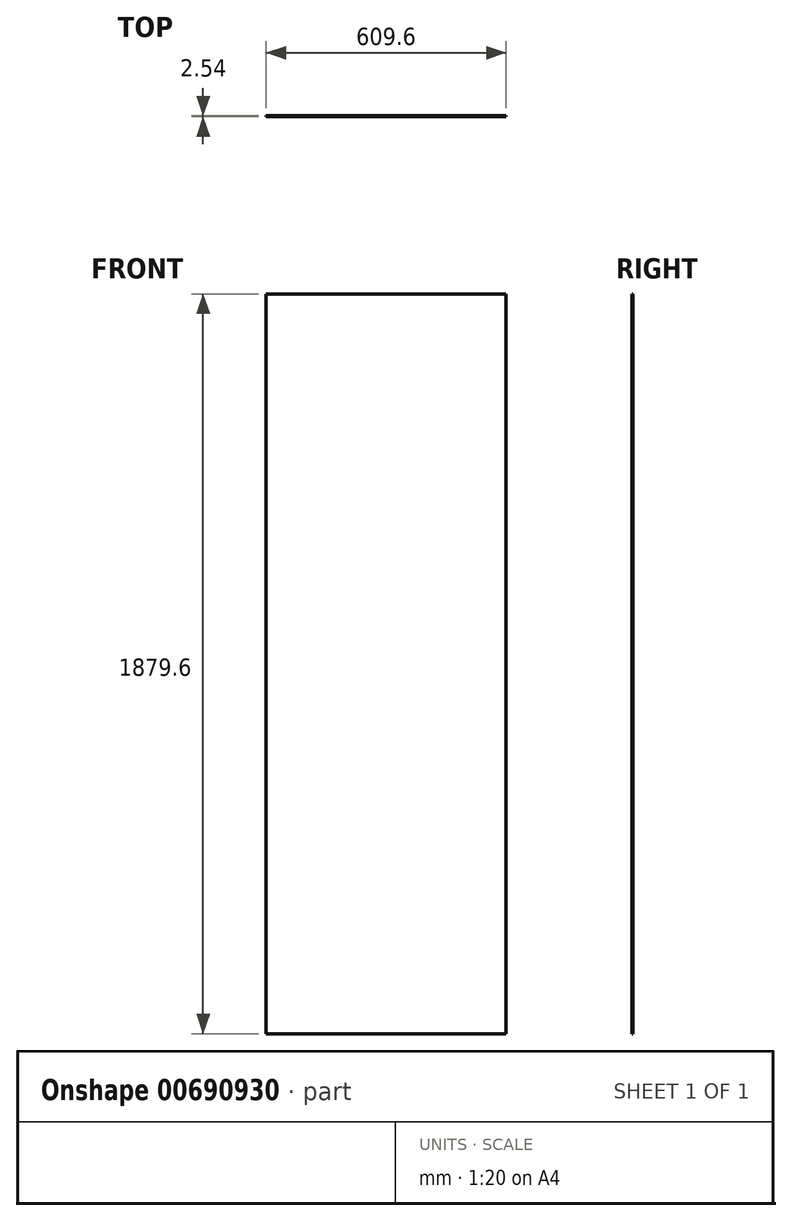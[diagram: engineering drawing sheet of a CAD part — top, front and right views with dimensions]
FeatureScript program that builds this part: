
annotation { "Feature Type Name" : "Feature", "Feature Type Description" : "" }
export const myFeature = defineFeature(function(context is Context, id is Id, definition is map)
    precondition{}
    {
        {
            var Q0;
            Q0=qCreatedBy(makeId("Front.planeOp"),FACE);
            var sketch = newSketch(context, id + "F0", { "sketchPlane" : qUnion([Q0])});
            skLineSegment(sketch, "E0.bottom", {"start": v(-303.05, 1450.8) * mm, "end": v(306.55, 1450.8) * mm});
            skLineSegment(sketch, "E0.top", {"start": v(-303.05, -428.8) * mm, "end": v(306.55, -428.8) * mm});
            skLineSegment(sketch, "E0.left", {"start": v(-303.05, 1450.8) * mm, "end": v(-303.05, -428.8) * mm});
            skLineSegment(sketch, "E0.right", {"start": v(306.55, 1450.8) * mm, "end": v(306.55, -428.8) * mm});
            skSolve(sketch);
        }
        {
            var Q0;
            Q0=makeQuery(id+"F0.imprint","IMPRINT",FACE,{"disambiguationData":[TD([[makeQuery(id+"F0.imprint","IMPRINT",EDGE,{"derivedFrom":sQuery(id+"F0.wireOp",EDGE,"E0.bottom")}),-1.0]])]});
            extrude(context, id + "F1", {"entities" : qUnion([Q0]), "depth" : 2.54 * mm, "offsetDistance" : 25.4 * mm});
        }
    });
